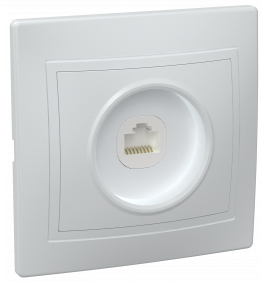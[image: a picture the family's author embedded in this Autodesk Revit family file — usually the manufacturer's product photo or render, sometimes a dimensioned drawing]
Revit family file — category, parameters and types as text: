
# Revit family: IEK_РозеткаКомпьютерная_Встраиваемая_Одноместная IP20_КВАРТА
name_source: partatom
category: Устройства связи
units: mm (PartAtom-declared; Revit-internal decimal feet)

## family parameters
Всегда вертикально = Да
На основе рабочей плоскости = Нет
Общий = Нет
При загрузке вырезать с полостями = Нет
Размер круглого соединителя = Использовать диаметр
Сохранять ориентацию аннотаций = Да
Тип детали = Нормальный
Точка расчета площади = Нет

## types (2) — shared parameters
ADSK_URL страницы изделия = https://www.iek.ru
ADSK_Версия Revit = 2019
ADSK_Версия семейства = 1.0
ADSK_Группирование = III ЭЛЕКТРОУСТАНОВОЧНЫЕ И ЭЛЕКТРОМОНТАЖНЫЕ ИЗДЕЛИЯ
ADSK_Единица измерения = шт
ADSK_Завод-изготовитель = IEK
ADSK_Марка = КВАРТА
ADSK_Материал наименование = Пластик
IEK_URL = https://www.iek.ru
IEK_Описание = Классический дизайн, проверенный временем и востребованный различными категориями потребителей, позволяет устанавливать изделия серии "КВАРТА" в квартирах, загородных домах, офисных и производственных помещениях.
IEK_Цена за единицу = 261.7
KSI_CMa_Строительные материалы = 01.7.14.03
Высота = 81 мм
Глубина = 43 мм
Изготовитель = IEK
Степень защиты = IP20
Тип монтажа = Встраиваемый
Ширина = 82 мм

## per-type parameters (varying)
| type | ADSK_Код изделия | ADSK_Масса | ADSK_Материал | ADSK_Наименование |
| РК10-КБ | EKK10-K01-DM | 0.083 | Цвет белый | Розетка 1-местная компьютерная РК10-КБ КВАРТА белый IEK |
| РК10-ККм | EKK10-K33-DM | 0.081 | Цвет кремовый | Розетка 1-местная компьютерная РК10-ККм КВАРТА кремовый IEK |
